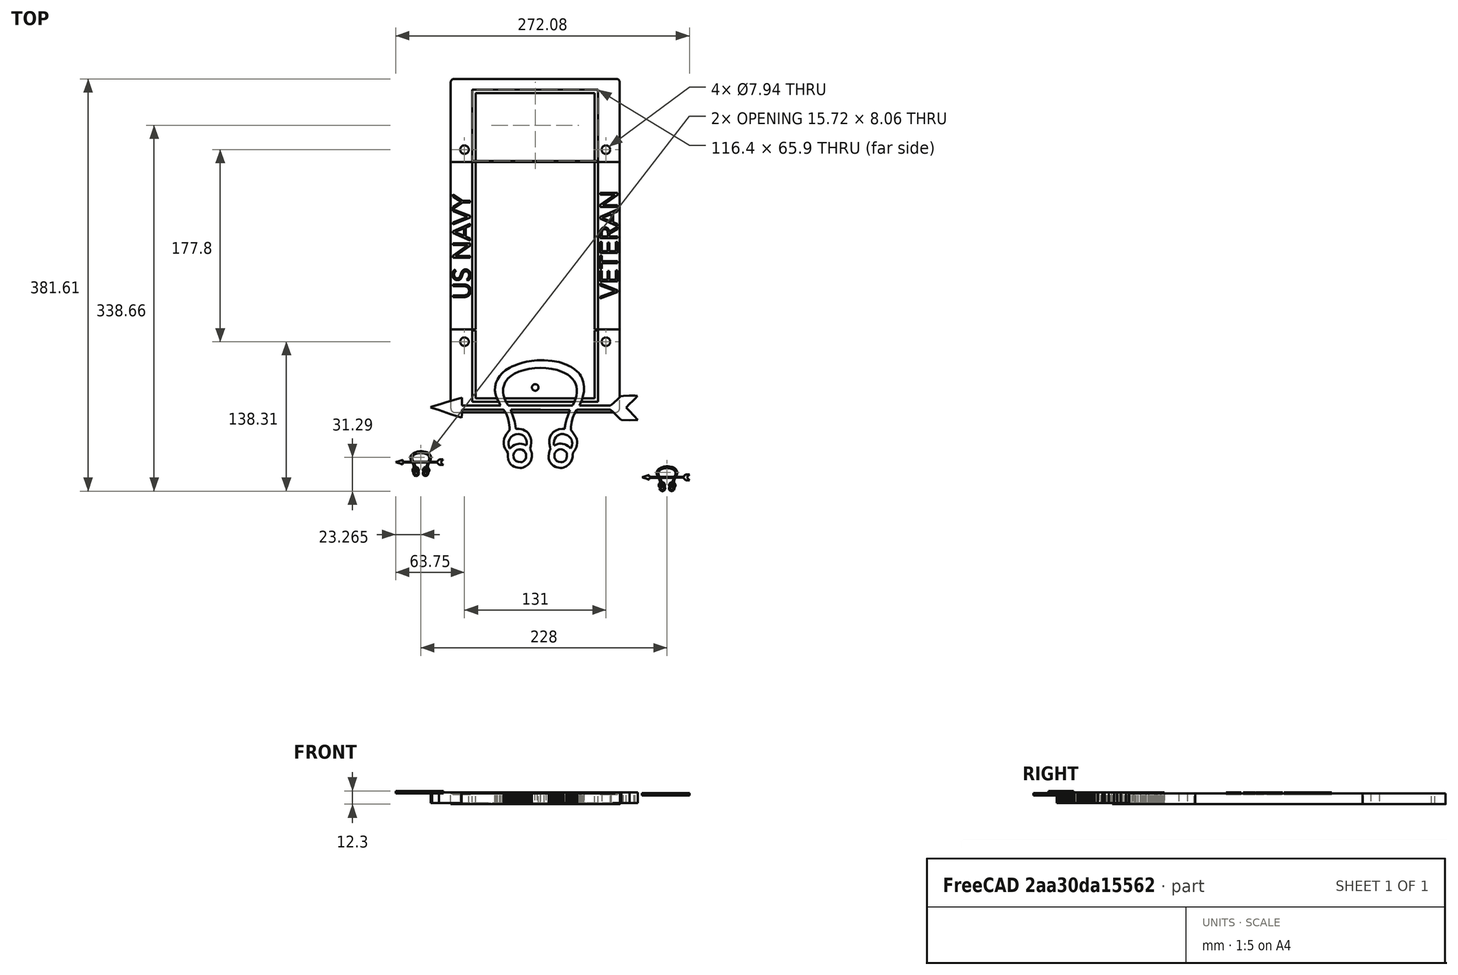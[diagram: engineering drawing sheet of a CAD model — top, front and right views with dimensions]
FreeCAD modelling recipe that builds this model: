
FCSTD DOCUMENT  (FreeCAD 0.22R36904 (Git))
Label: Frame-CNC
License: All rights reserved
LicenseURL: http://en.wikipedia.org/wiki/All_rights_reserved
objects: Part::Feature×5, Sketcher::SketchObject×4, PartDesign::Pad×4, PartDesign::Body×4, Part::Part2DObjectPython×2, Part::Extrusion×2, Spreadsheet::Sheet×1, Mesh::Feature×1, PartDesign::AdditiveBox×1, PartDesign::SubtractiveCylinder×1, PartDesign::LinearPattern×1
note: 30 computed .brp shape members not serialized (recipe doc carries the construction recipe); baked Part::Feature solids carry a one-line shape summary decoded from their .brp

FEATURE [Part::Part2DObjectPython] ShapeString  # Draft 2D object (typed FeaturePython)
  FontFile = /System/Library/Fonts/Avenir.ttc
  Fuse = false
  Justification = 4
  JustificationReference = 0
  KeepLeftMargin = false
  MakeFace = true
  ObliqueAngle = 0
  Placement = pos=(-68.2,154.4,10) rot=(0,0,1;1.5708rad)
  ScaleToSize = true
  Size = 16
  String = US NAVY
  Tracking = 1
  expr: .Placement.Base.x = -(<<vars>>.width - <<vars>>.top_banner_width) / 2
  expr: .Placement.Base.y = 152.13 + 2.27
  expr: .Placement.Base.z = <<vars>>.height
  expr: Size = <<vars>>.font_size
FEATURE [Spreadsheet::Sheet] Spreadsheet  label="vars"
  cells = A1='Length; B1(length)=308.8; C1==B1 / 2; D1='plate hole; E1(plate_hole)=7.9375; A2='Width; B2(width)=156.4; C2=160; D2='plate hole top left distance; E2(plate_hole_vertical)==length / 2 - 177.8 / 2; A3='material length; B3(material_length)=310; D3='plate hole horizontal_right; E3(plate_hole_horizontal_right)==(length - hole_distance_horizontal) / 2; A4='material_width; B4(material_width)=160; D4='plate hole horizontal left; E4(plate_hole_horizontal_left)==length / 2 - 88.9; A5='Font Size; B5(font_size)=16; D5='hole distance horizontal; E5(hole_distance_horizontal)=177.8; A6='Top banner width; B6(top_banner_width)=20; D6='hole distance vertical; E6(hole_distance_vertical)=120.65; A7='Bottom banner witdh; B7(bottom_banner_width)=20; A8='Height; B8(height)=10; A9='Guide hole distance; B9(guide_hole_length)=120; A10='Guide hole width; B10(guide_hole_width)=130; A11='hole distance from edge; B11(hole_distance_from_edge)=20; A12='hole size; B12(hole_size)=6.05; A13='template_length; B13(template_length)=155; A14='reference point; B14(reference_point)==first_cut; C14(second_cut)==(length - template_length) / 2 + template_length; D14(third_cut)==(length - template_length) / 2; E14(first_cut)==length; A15='side_width; B15(side_width)=10; A16='bit size; B16(bit_size)=3.175; A17='bridge width; B17(bridge_width)=1
FEATURE [Part::Part2DObjectPython] ShapeString001  # Draft 2D object (typed FeaturePython)
  FontFile = /System/Library/Fonts/Avenir.ttc
  Fuse = false
  Justification = 4
  JustificationReference = 0
  KeepLeftMargin = false
  MakeFace = true
  ObliqueAngle = 0
  Placement = pos=(68.2,154.395,10) rot=(0,0,1;1.5708rad)
  ScaleToSize = true
  Size = 16
  String = VETERAN
  Tracking = 0
  expr: .Placement.Base.x = (<<vars>>.width - <<vars>>.bottom_banner_width) / 2
  expr: .Placement.Base.y = 151.53 + 2.865
  expr: .Placement.Base.z = <<vars>>.height
  expr: Size = <<vars>>.font_size
FEATURE [Mesh::Feature] Sonar_Tech
FEATURE [Part::Feature] Sonar_Tech001
  Placement = pos=(0,0,10) rot=(0,0,1;0rad)
  shape: bbox 191.7 x 99.71 x 10 mm, 1500 faces, 0 solids (baked)
FEATURE [Part::Feature] Shell
  Placement = pos=(0,0,10) rot=(0,0,1;0rad)
  shape: bbox 191.7 x 99.71 x 10 mm, 373 faces, 0 solids (baked)
  expr: .Placement.Base.z = <<vars>>.height
FEATURE [Part::Feature] Scale_solid  label="Scale (Solid)"
  Placement = pos=(13,14,9) rot=(0,0,1;0rad)
  shape: bbox 44.08 x 22.93 x 2.3 mm, 373 faces (baked)
FEATURE [Part::Feature] Scale001_solid  label="Scale001 (Solid)"
  Placement = pos=(0,0,7) rot=(0,0,1;0rad)
  shape: bbox 44.08 x 22.93 x 2.3 mm, 373 faces (baked)
FEATURE [Sketcher::SketchObject] Sketch
  FullyConstrained = true
  MapMode = 5
  expr: Constraints[13] = <<vars>>.width / 2
  expr: Constraints[14] = <<vars>>.width
  expr: Constraints[23] = <<vars>>.top_banner_width
  expr: Constraints[24] = <<vars>>.bottom_banner_width
  expr: Constraints[25] = (<<vars>>.length - <<vars>>.template_length) / 2
  expr: Constraints[29] = <<vars>>.length + 10
  expr: Constraints[30] = (<<vars>>.length - <<vars>>.template_length) / 2 - <<vars>>.side_width - <<vars>>.bridge_width
  expr: Constraints[32] = <<vars>>.plate_hole
  expr: Constraints[33] = <<vars>>.plate_hole
  expr: Constraints[34] = <<vars>>.plate_hole_vertical
  expr: Constraints[35] = <<vars>>.plate_hole_vertical
  expr: Constraints[36] = <<vars>>.plate_hole_horizontal_left
  expr: Constraints[37] = <<vars>>.plate_hole_horizontal_left
  expr: Constraints[38] = <<vars>>.reference_point + 10
  expr: Constraints[39] = <<vars>>.reference_point + <<vars>>.side_width + 10
  sketch-geometry (13):
    g0: LineSegment StartX=78.2 StartY=76.9 StartZ=0 EndX=-78.2 EndY=76.9 EndZ=0
    g1: LineSegment StartX=-78.2 StartY=76.9 StartZ=0 EndX=-78.2 EndY=4 EndZ=0
    g2: ArcOfCircle CenterX=-74.2 CenterY=4 CenterZ=0 NormalX=0 NormalY=0 NormalZ=1 AngleXU=0 Radius=4 StartAngle=3.14159 EndAngle=4.71239
    g3: LineSegment StartX=-74.2 StartY=3e-16 StartZ=0 EndX=74.2 EndY=3e-16 EndZ=0
    g4: ArcOfCircle CenterX=74.2 CenterY=4 CenterZ=0 NormalX=0 NormalY=0 NormalZ=1 AngleXU=0 Radius=4 StartAngle=4.71239 EndAngle=6.28319
    g5: LineSegment StartX=78.2 StartY=4 StartZ=0 EndX=78.2 EndY=76.9 EndZ=0
    g6: LineSegment StartX=58.2 StartY=75.9 StartZ=0 EndX=-58.2 EndY=75.9 EndZ=0
    g7: LineSegment StartX=58.2 StartY=75.9 StartZ=0 EndX=58.2 EndY=10 EndZ=0
    g8: LineSegment StartX=58.2 StartY=10 StartZ=0 EndX=-58.2 EndY=10 EndZ=0
    g9: LineSegment StartX=-58.2 StartY=10 StartZ=0 EndX=-58.2 EndY=75.9 EndZ=0
    g10: GeomPoint X=0 Y=-318.8 Z=0
    g11: Circle CenterX=-65.5 CenterY=65.5 CenterZ=0 NormalX=0 NormalY=0 NormalZ=1 AngleXU=0 Radius=3.96875
    g12: Circle CenterX=65.5 CenterY=65.5 CenterZ=0 NormalX=0 NormalY=0 NormalZ=1 AngleXU=0 Radius=3.96875
  constraints (40):
    c: Vertical(g1)
    c: Coincident(g2,g3)
    c: Horizontal(g3)
    c: Tangent(g3,g4) = -1.5708
    c: Coincident(g4,g5)
    c: Vertical(g5)
    c: Horizontal(g8)
    c: Vertical(g9)
    c: Horizontal(g6)
    c: Vertical(g7)
    c: Equal(g2,g4)
    c: Angle(g2) = 1.5708
    c: Angle(g4) = 1.5708
    c: DistanceX(g0,g-1) = 78.2
    c: DistanceX(g0,g5) = 156.4
    c: Equal(g1,g5)
    c: Coincident(g2,g1)
    c: Horizontal(g0)
    c: DistanceX(g2) = -74.2
    c: Coincident(g1,g0)
    c: Coincident(g0,g5)
    c: Coincident(g9,g6)
    c: Coincident(g6,g7)
    c: Distance(g6,g1) = 20
    c: Distance(g6,g5) = 20
    c: Distance(g2,g0) = 76.9
    c: Coincident(g7,g8)
    c: Coincident(g9,g8)
    c: PointOnObject(g10,g-2)
    c: Distance(g-1,g10) = 318.8
    c: DistanceY(g9,g9) = 65.9
    c: DistanceY(g-1,g-1) = 0
    c: Diameter(g11) = 7.9375
    c: Diameter(g12) = 7.9375
    c: DistanceX(g11,g-1) = 65.5
    c: DistanceX(g-1,g12) = 65.5
    c: Distance(g11,g3) = 65.5
    c: Distance(g12,g3) = 65.5
    c: Distance(g10,g3) = 318.8
    c: Distance(g10,g8) = 328.8
FEATURE [PartDesign::Pad] Pad
  Direction = (0,0,1)
  Length = 10
  Length2 = 10
  Profile = -> Sketch
  ReferenceAxis = -> Sketch [N_Axis]
  Suppressed = false
  Type = 0
  expr: Length = <<vars>>.height
FEATURE [PartDesign::AdditiveBox] Box
  AttacherType = Attacher::AttachEngine3D
  AttachmentOffset = pos=(-55.025,13.175,0) rot=(0,0,1;0rad)
  AttachmentSupport = -> [XY_Plane]
  BaseFeature = -> Pad
  Height = 10
  Length = 110.05
  MapMode = 5
  Placement = pos=(-55.025,13.175,0) rot=(0,0,1;0rad)
  Suppressed = false
  Width = 282.45
  expr: .AttachmentOffset.Base.x = -<<vars>>.width / 2 + <<vars>>.top_banner_width + <<vars>>.bit_size
  expr: .AttachmentOffset.Base.y = <<vars>>.reference_point - <<vars>>.length + <<vars>>.side_width + <<vars>>.bit_size
  expr: Height = <<vars>>.height
  expr: Length = <<vars>>.width - <<vars>>.top_banner_width - <<vars>>.bottom_banner_width - <<vars>>.bit_size * 2
  expr: Width = <<vars>>.length - <<vars>>.side_width * 2 - <<vars>>.bit_size * 2
FEATURE [Sketcher::SketchObject] Sketch001
  FullyConstrained = true
  MapMode = 5
  expr: Constraints[18] = <<vars>>.width
  expr: Constraints[23] = <<vars>>.top_banner_width
  expr: Constraints[24] = <<vars>>.bottom_banner_width
  expr: Constraints[25] = -<<vars>>.width / 2
  expr: Constraints[26] = (<<vars>>.length - <<vars>>.template_length) / 2
  expr: Constraints[28] = <<vars>>.plate_hole
  expr: Constraints[30] = <<vars>>.plate_hole_vertical
  expr: Constraints[31] = <<vars>>.plate_hole_vertical
  expr: Constraints[32] = <<vars>>.plate_hole_horizontal_right
  expr: Constraints[34] = <<vars>>.length + <<vars>>.reference_point
  expr: Constraints[35] = <<vars>>.length
  expr: Constraints[36] = <<vars>>.length - <<vars>>.side_width + <<vars>>.reference_point
  expr: Constraints[37] = <<vars>>.length - (<<vars>>.length - <<vars>>.template_length) / 2 + <<vars>>.bridge_width + <<vars>>.reference_point
  sketch-geometry (13):
    g0: LineSegment StartX=-78.2 StartY=231.9 StartZ=0 EndX=-78.2 EndY=305.8 EndZ=0
    g1: ArcOfCircle CenterX=-75.2 CenterY=305.8 CenterZ=0 NormalX=0 NormalY=0 NormalZ=1 AngleXU=0 Radius=3 StartAngle=1.5708 EndAngle=3.14159
    g2: LineSegment StartX=-75.2 StartY=308.8 StartZ=0 EndX=75.2 EndY=308.8 EndZ=0
    g3: ArcOfCircle CenterX=75.2 CenterY=305.8 CenterZ=0 NormalX=0 NormalY=0 NormalZ=1 AngleXU=0 Radius=3 StartAngle=3.8e-15 EndAngle=1.5708
    g4: LineSegment StartX=78.2 StartY=305.8 StartZ=0 EndX=78.2 EndY=231.9 EndZ=0
    g5: LineSegment StartX=78.2 StartY=231.9 StartZ=0 EndX=-78.2 EndY=231.9 EndZ=0
    g6: LineSegment StartX=-58.2 StartY=232.9 StartZ=0 EndX=58.2 EndY=232.9 EndZ=0
    g7: LineSegment StartX=58.2 StartY=232.9 StartZ=0 EndX=58.2 EndY=298.8 EndZ=0
    g8: LineSegment StartX=58.2 StartY=298.8 StartZ=0 EndX=-58.2 EndY=298.8 EndZ=0
    g9: LineSegment StartX=-58.2 StartY=298.8 StartZ=0 EndX=-58.2 EndY=232.9 EndZ=0
    g10: Circle CenterX=-65.5 CenterY=243.3 CenterZ=0 NormalX=0 NormalY=0 NormalZ=1 AngleXU=0 Radius=3.96875
    g11: Circle CenterX=65.5 CenterY=243.3 CenterZ=0 NormalX=0 NormalY=0 NormalZ=1 AngleXU=0 Radius=3.96875
    g12: GeomPoint X=0 Y=-308.8 Z=0
  constraints (38):
    c: Tangent(g0,g1) = 1.5708
    c: Coincident(g1,g2)
    c: Horizontal(g2)
    c: Tangent(g2,g3) = 1.5708
    c: Coincident(g3,g4)
    c: Vertical(g4)
    c: Coincident(g4,g5)
    c: Coincident(g5,g0)
    c: Horizontal(g5)
    c: Coincident(g6,g7)
    c: Coincident(g7,g8)
    c: Coincident(g8,g9)
    c: Coincident(g9,g6)
    c: Horizontal(g6)
    c: Horizontal(g8)
    c: Vertical(g7)
    c: Vertical(g9)
    c: Vertical(g0)
    c: DistanceX(g5,g5) = 156.4
    c: Angle(g1) = 1.5708
    c: Angle(g3) = 1.5708
    c: Diameter(g1) = 6
    c: Diameter(g3) = 6
    c: Distance(g6,g0) = 20
    c: Distance(g6,g4) = 20
    c: DistanceX(g-2,g0) = -78.2
    c: Distance(g4,g2) = 76.9
    c: Equal(g11,g10)
    c: Diameter(g11) = 7.9375
    c: Horizontal(g10,g11)
    c: DistanceX(g10,g-1) = 65.5
    c: DistanceX(g-1,g11) = 65.5
    c: Distance(g10,g2) = 65.5
    c: PointOnObject(g12,g-2)
    c: Distance(g12,g2) = 617.6
    c: DistanceY(g12,g-1) = 308.8
    c: Distance(g12,g8) = 607.6
    c: Distance(g12,g6) = 541.7
FEATURE [PartDesign::Pad] Pad001
  Direction = (0,0,1)
  Length = 10
  Length2 = 10
  Profile = -> Sketch001
  ReferenceAxis = -> Sketch001 [N_Axis]
  Suppressed = false
  Type = 0
  expr: Length = <<vars>>.height
FEATURE [PartDesign::Body] Body001
  Group = -> [Sketch001,Pad001]
  Origin = -> Origin001
  Tip = -> Pad001
FEATURE [Part::Feature] Sonar_Tech001_solid  label="Sonar_Tech001 (Solid)"
  Placement = pos=(0,0,1) rot=(0,0,1;0rad)
  shape: bbox 191.7 x 99.71 x 10 mm, 1500 faces (baked)
FEATURE [Part::Extrusion] Extrude
  Base = -> ShapeString
  Dir = (0,0,1)
  DirMode = 2
  FaceMakerClass = Part::FaceMakerBullseye
  LengthFwd = 2
  LengthRev = 0
  Solid = false
  Symmetric = true
FEATURE [Part::Extrusion] Extrude001
  Base = -> ShapeString001
  Dir = (0,0,1)
  DirMode = 2
  FaceMakerClass = Part::FaceMakerBullseye
  LengthFwd = 2
  LengthRev = 0
  Solid = false
  Symmetric = true
FEATURE [Sketcher::SketchObject] Sketch002
  FullyConstrained = true
  MapMode = 5
  expr: Constraints[10] = -<<vars>>.width / 2
  expr: Constraints[12] = <<vars>>.length
  expr: Constraints[13] = (<<vars>>.length - <<vars>>.template_length) / 2 + <<vars>>.reference_point
  expr: Constraints[8] = <<vars>>.top_banner_width
  expr: Constraints[9] = <<vars>>.template_length
  sketch-geometry (5):
    g0: LineSegment StartX=-78.2 StartY=231.9 StartZ=0 EndX=-78.2 EndY=76.9 EndZ=0
    g1: LineSegment StartX=-78.2 StartY=76.9 StartZ=0 EndX=-58.2 EndY=76.9 EndZ=0
    g2: LineSegment StartX=-58.2 StartY=76.9 StartZ=0 EndX=-58.2 EndY=231.9 EndZ=0
    g3: LineSegment StartX=-58.2 StartY=231.9 StartZ=0 EndX=-78.2 EndY=231.9 EndZ=0
    g4: GeomPoint X=0 Y=-308.8 Z=0
  constraints (14):
    c: Coincident(g0,g1)
    c: Coincident(g1,g2)
    c: Coincident(g2,g3)
    c: Coincident(g3,g0)
    c: Vertical(g0)
    c: Vertical(g2)
    c: Horizontal(g1)
    c: Horizontal(g3)
    c: DistanceX(g3,g3) = 20
    c: DistanceY(g0,g0) = 155
    c: DistanceX(g-2,g0) = -78.2
    c: PointOnObject(g4,g-2)
    c: DistanceY(g4,g-1) = 308.8
    c: DistanceY(g4,g1) = 385.7
FEATURE [PartDesign::Pad] Pad002
  Direction = (0,0,1)
  Length = 10
  Length2 = 10
  Profile = -> Sketch002
  ReferenceAxis = -> Sketch002 [N_Axis]
  Suppressed = false
  Type = 0
  expr: Length = <<vars>>.height
FEATURE [PartDesign::Body] Body002
  Group = -> [Sketch002,Pad002]
  Origin = -> Origin002
  Tip = -> Pad002
FEATURE [Sketcher::SketchObject] Sketch003
  FullyConstrained = true
  MapMode = 5
  expr: Constraints[11] = <<vars>>.length
  expr: Constraints[12] = <<vars>>.width / 2
  expr: Constraints[13] = (<<vars>>.length - <<vars>>.template_length) / 2 + <<vars>>.reference_point
  expr: Constraints[8] = <<vars>>.bottom_banner_width
  expr: Constraints[9] = <<vars>>.template_length
  sketch-geometry (5):
    g0: LineSegment StartX=58.2 StartY=231.9 StartZ=0 EndX=58.2 EndY=76.9 EndZ=0
    g1: LineSegment StartX=58.2 StartY=76.9 StartZ=0 EndX=78.2 EndY=76.9 EndZ=0
    g2: LineSegment StartX=78.2 StartY=76.9 StartZ=0 EndX=78.2 EndY=231.9 EndZ=0
    g3: LineSegment StartX=78.2 StartY=231.9 StartZ=0 EndX=58.2 EndY=231.9 EndZ=0
    g4: GeomPoint X=0 Y=-308.8 Z=0
  constraints (14):
    c: Coincident(g0,g1)
    c: Coincident(g1,g2)
    c: Coincident(g2,g3)
    c: Coincident(g3,g0)
    c: Vertical(g0)
    c: Vertical(g2)
    c: Horizontal(g1)
    c: Horizontal(g3)
    c: DistanceX(g3,g3) = 20
    c: DistanceY(g2,g2) = 155
    c: PointOnObject(g4,g-2)
    c: DistanceY(g4,g-1) = 308.8
    c: DistanceX(g-1,g2) = 78.2
    c: DistanceY(g4,g0) = 385.7
FEATURE [PartDesign::Pad] Pad003
  Direction = (0,0,1)
  Length = 10
  Length2 = 10
  Profile = -> Sketch003
  ReferenceAxis = -> Sketch003 [N_Axis]
  Suppressed = false
  Type = 0
  expr: Length = <<vars>>.height
FEATURE [PartDesign::Body] Body003
  Group = -> [Sketch003,Pad003]
  Origin = -> Origin003
  Tip = -> Pad003
FEATURE [PartDesign::SubtractiveCylinder] Cylinder
  Angle = 360
  AttacherType = Attacher::AttachEngine3D
  AttachmentOffset = pos=(55.025,10,-10) rot=(0,0,1;0rad)
  AttachmentSupport = -> [Box]
  BaseFeature = -> Box
  FirstAngle = 0
  Height = 10
  MapMode = 5
  Placement = pos=(0,23.175,0) rot=(0,0,1;0rad)
  Radius = 3.03
  SecondAngle = 0
  Suppressed = false
  expr: .AttachmentOffset.Base.x = Box.Length / 2
  expr: .AttachmentOffset.Base.y = <<vars>>.side_width
  expr: .AttachmentOffset.Base.z = -Height
  expr: Height = <<vars>>.height
  expr: Radius = 3.03
FEATURE [PartDesign::LinearPattern] LinearPattern
  BaseFeature = -> Cylinder
  Direction = -> Y_Axis
  Length = 75.91
  Mode = 1
  Occurrences = 2
  Offset = 75.91
  Originals = -> [Cylinder]
  Placement = pos=(0,23.175,0) rot=(0,0,1;0rad)
  Suppressed = false
  expr: Offset = 75.91 mm
FEATURE [PartDesign::Body] Body
  Group = -> [Sketch,Pad,Box,Cylinder,LinearPattern]
  Origin = -> Origin
  Tip = -> Cylinder
